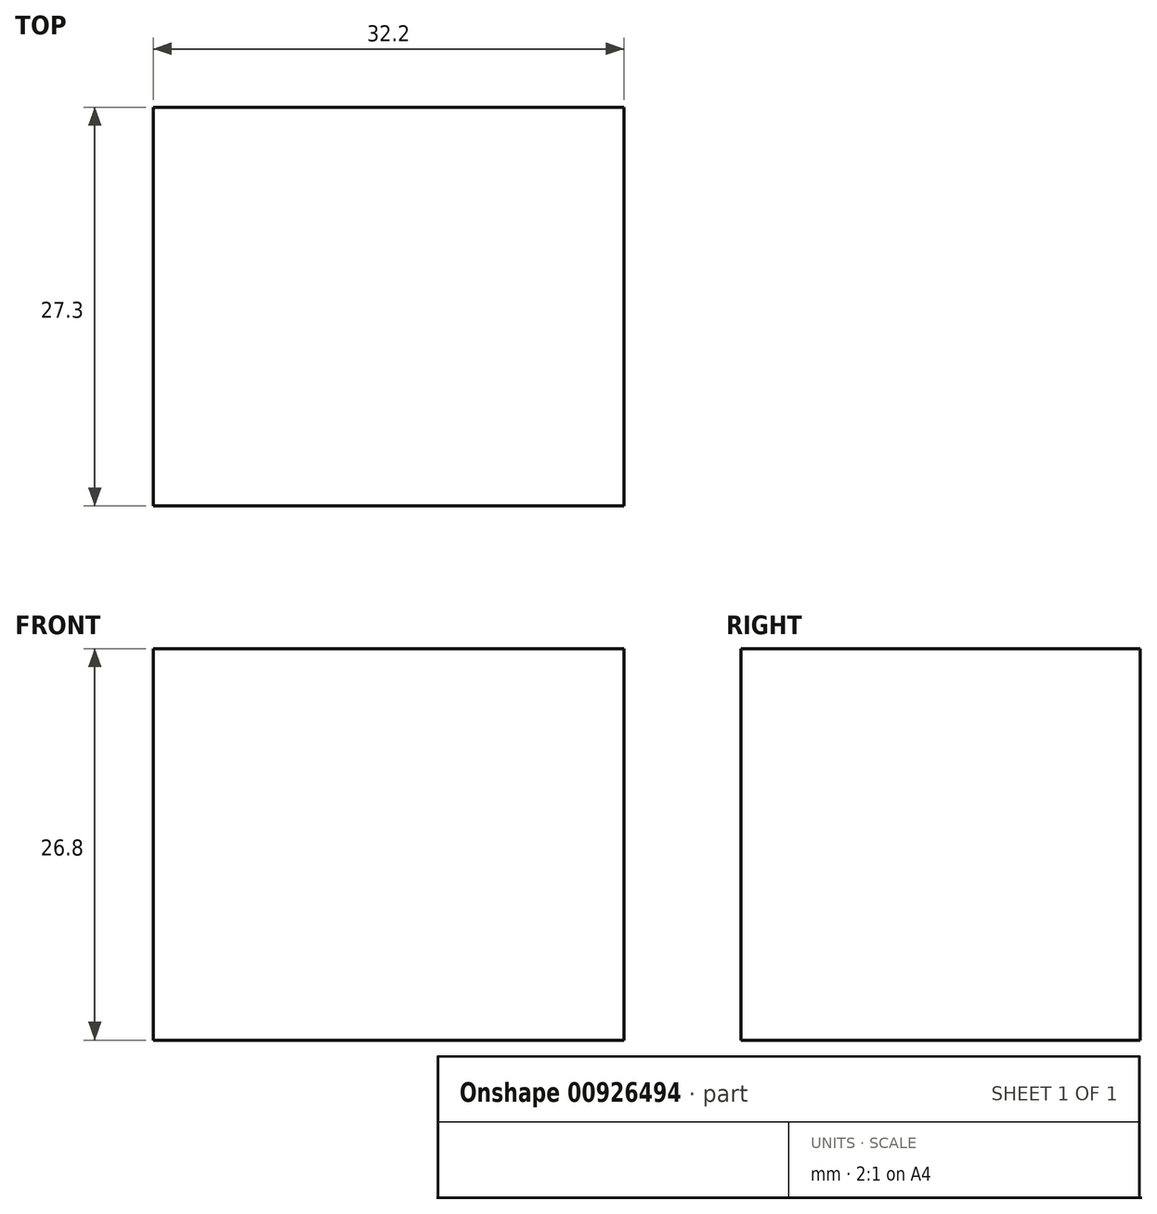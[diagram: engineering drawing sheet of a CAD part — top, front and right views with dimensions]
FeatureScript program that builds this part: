
annotation { "Feature Type Name" : "Feature", "Feature Type Description" : "" }
export const myFeature = defineFeature(function(context is Context, id is Id, definition is map)
    precondition{}
    {
        {
            var Q0;
            Q0=qCreatedBy(makeId("Top.planeOp"),FACE);
            var sketch = newSketch(context, id + "F0", { "sketchPlane" : qUnion([Q0])});
            skLineSegment(sketch, "E0.bottom", {"start": v(0, 0) * mm, "end": v(32.2, 0) * mm});
            skLineSegment(sketch, "E0.top", {"start": v(0, 27.3) * mm, "end": v(32.2, 27.3) * mm});
            skLineSegment(sketch, "E0.left", {"start": v(0, 0) * mm, "end": v(0, 27.3) * mm});
            skLineSegment(sketch, "E0.right", {"start": v(32.2, 0) * mm, "end": v(32.2, 27.3) * mm});
            skSolve(sketch);
        }
        {
            var Q0;
            Q0 = qSketchRegion(id + "F0", true);
            extrude(context, id + "F1", {"entities" : qUnion([Q0]), "depth" : 26.8 * mm, "offsetDistance" : 25 * mm});
        }
    });
